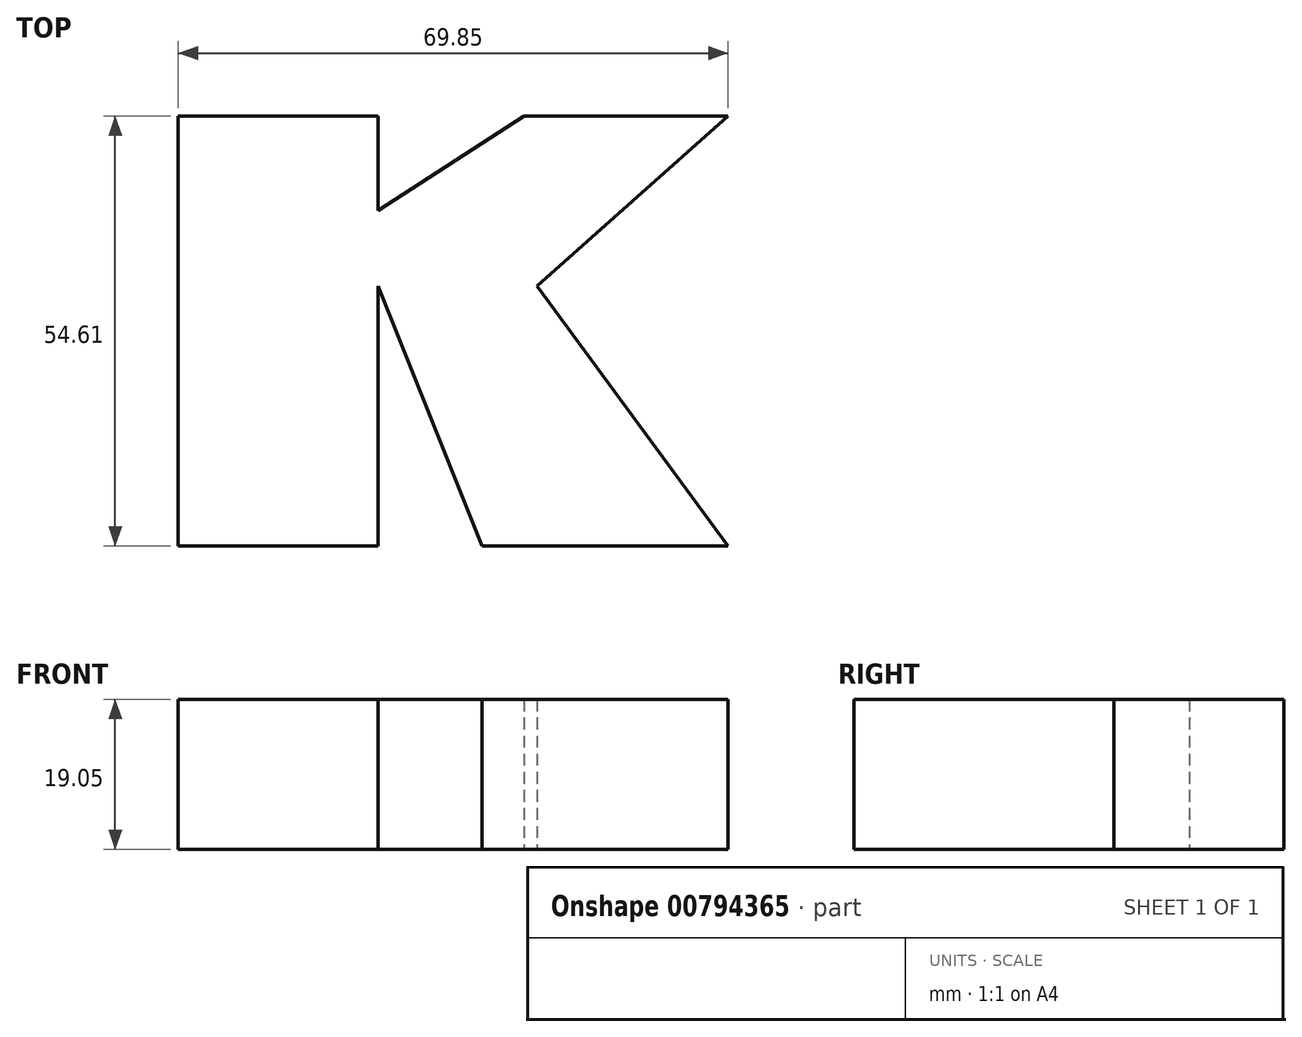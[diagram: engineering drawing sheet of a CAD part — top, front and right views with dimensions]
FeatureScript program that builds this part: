
annotation { "Feature Type Name" : "Feature", "Feature Type Description" : "" }
export const myFeature = defineFeature(function(context is Context, id is Id, definition is map)
    precondition{}
    {
        {
            var Q0;
            Q0=qCreatedBy(makeId("Top.planeOp"),FACE);
            var sketch = newSketch(context, id + "F0", { "sketchPlane" : qUnion([Q0])});
            skLineSegment(sketch, "E0", {"start": v(-32.17, 14.88) * mm, "end": v(37.68, 14.88) * mm});
            skLineSegment(sketch, "E1", {"start": v(-32.17, 14.88) * mm, "end": v(-32.17, -39.73) * mm});
            skLineSegment(sketch, "E2", {"start": v(-32.17, -39.73) * mm, "end": v(-6.77, -39.73) * mm});
            skLineSegment(sketch, "E3", {"start": v(-6.77, -39.73) * mm, "end": v(-6.77, -6.71) * mm});
            skLineSegment(sketch, "E4", {"start": v(37.68, 14.88) * mm, "end": v(11.78, 14.88) * mm});
            skLineSegment(sketch, "E5", {"start": v(11.78, 14.88) * mm, "end": v(-6.77, 2.88) * mm});
            skLineSegment(sketch, "E6", {"start": v(-6.77, 2.88) * mm, "end": v(-6.77, 14.88) * mm});
            skLineSegment(sketch, "E7", {"start": v(-32.17, 14.88) * mm, "end": v(-6.77, 14.88) * mm});
            skLineSegment(sketch, "E8", {"start": v(-6.77, -6.71) * mm, "end": v(6.43, -39.73) * mm});
            skLineSegment(sketch, "E9", {"start": v(6.43, -39.73) * mm, "end": v(37.68, -39.73) * mm});
            skLineSegment(sketch, "E10", {"start": v(37.68, -39.73) * mm, "end": v(13.43, -6.71) * mm});
            skLineSegment(sketch, "E11", {"start": v(37.68, 14.88) * mm, "end": v(13.43, -6.71) * mm});
            skSolve(sketch);
        }
        {
            var Q0;
            Q0=makeQuery(id+"F0.imprint","IMPRINT",FACE,{"disambiguationData":[TD([[makeQuery(id+"F0.imprint","IMPRINT",EDGE,{"derivedFrom":sQuery(id+"F0.wireOp",EDGE,"E1")}),1.0]])]});
            extrude(context, id + "F1", {"entities" : qUnion([Q0]), "depth" : 19.05 * mm, "offsetDistance" : 25.4 * mm});
        }
    });
